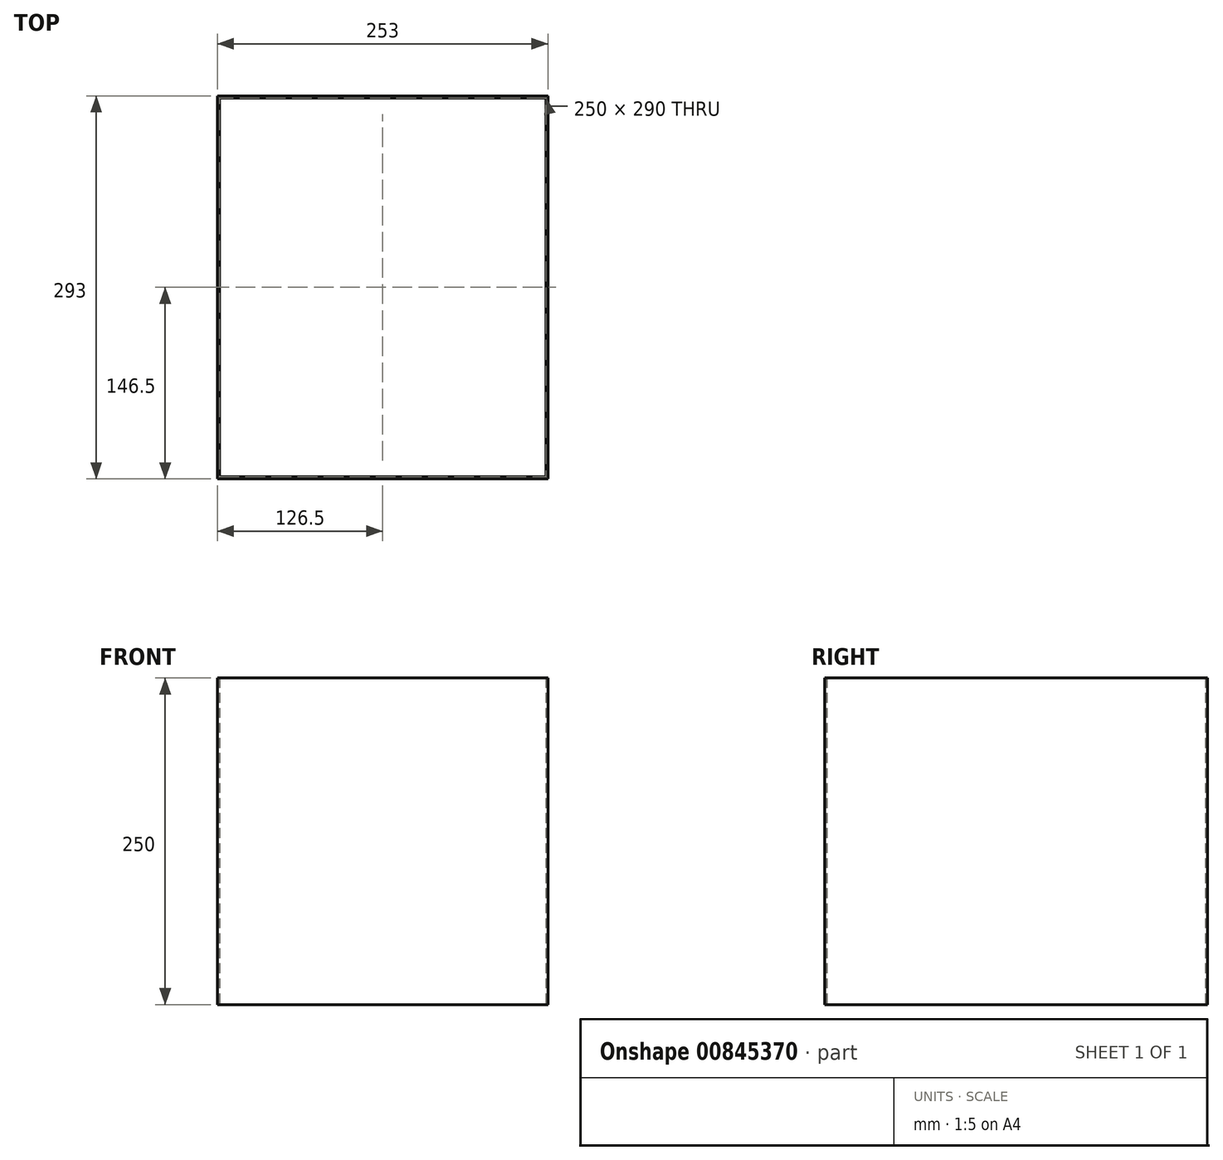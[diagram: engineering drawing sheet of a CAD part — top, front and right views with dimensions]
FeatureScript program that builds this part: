
annotation { "Feature Type Name" : "Feature", "Feature Type Description" : "" }
export const myFeature = defineFeature(function(context is Context, id is Id, definition is map)
    precondition{}
    {
        {
            var Q0;
            Q0=qCreatedBy(makeId("Top.planeOp"),FACE);
            var sketch = newSketch(context, id + "F0", { "sketchPlane" : qUnion([Q0])});
            skLineSegment(sketch, "E0.bottom", {"start": v(125, -145) * mm, "end": v(-125, -145) * mm});
            skLineSegment(sketch, "E0.top", {"start": v(125, 145) * mm, "end": v(-125, 145) * mm});
            skLineSegment(sketch, "E0.left", {"start": v(125, -145) * mm, "end": v(125, 145) * mm});
            skLineSegment(sketch, "E0.right", {"start": v(-125, -145) * mm, "end": v(-125, 145) * mm});
            skPoint(sketch, "E0.middle", {"position": v(0, 0) * mm});
            skLineSegment(sketch, "E1.bottom", {"start": v(126.5, -146.5) * mm, "end": v(-126.5, -146.5) * mm});
            skLineSegment(sketch, "E1.top", {"start": v(126.5, 146.5) * mm, "end": v(-126.5, 146.5) * mm});
            skLineSegment(sketch, "E1.left", {"start": v(126.5, -146.5) * mm, "end": v(126.5, 146.5) * mm});
            skLineSegment(sketch, "E1.right", {"start": v(-126.5, -146.5) * mm, "end": v(-126.5, 146.5) * mm});
            skSolve(sketch);
        }
        {
            var Q0;
            Q0 = qSketchRegion(id + "F0", true);
            extrude(context, id + "F1", {"entities" : qUnion([Q0]), "depth" : 250 * mm, "offsetDistance" : 25 * mm});
        }
    });
